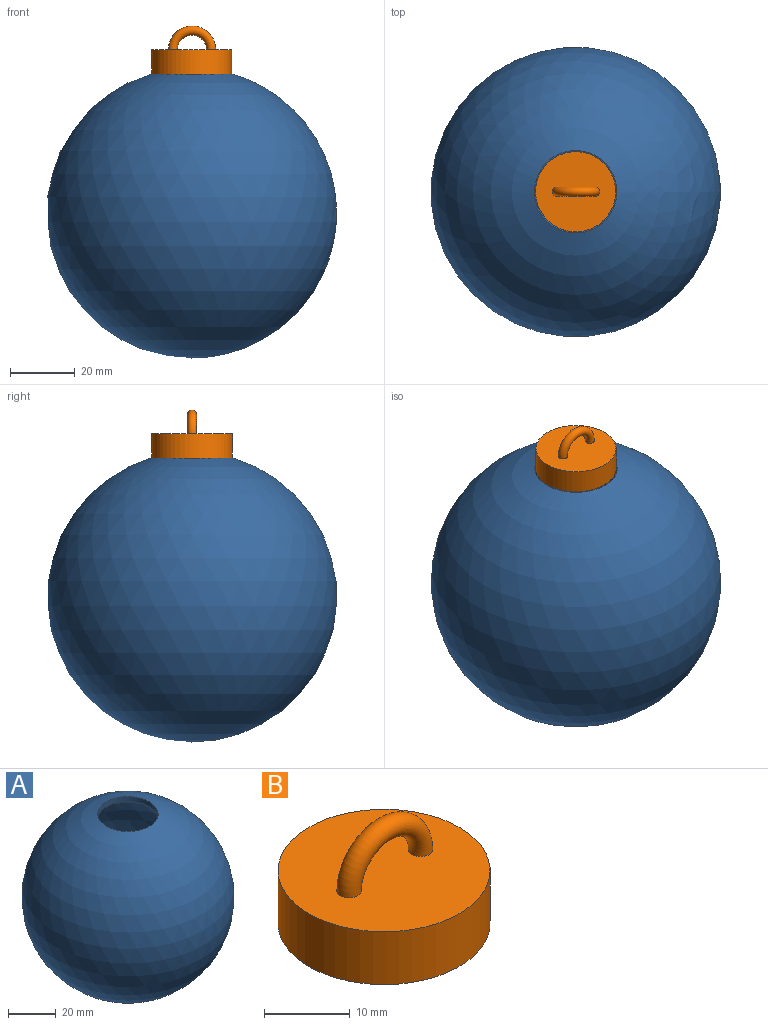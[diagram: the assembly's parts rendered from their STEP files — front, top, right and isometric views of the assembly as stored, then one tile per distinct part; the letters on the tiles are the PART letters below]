
ASSEMBLY  parts=2 mates=1
PART A: 3 faces, bbox 89.3x89.3x87.5 mm
  f0: sphere r=42.25mm, area 21911.1mm2, adj f2
  f1: sphere r=44.66mm, area 24548.8mm2, adj f2
  f2: cylinder r=12.7mm len=25.4mm, axis (0,0,1), area 201.4mm2, adj f0,f1
PART B: 4 faces, bbox 24.7x24.7x15.4 mm
  f0: plane 24.68x24.68mm, normal (0,0,1), area 465.8mm2, adj f1,f3
  f1: cylinder r=12.34mm len=24.68mm, axis (0,0,1), area 583.8mm2, adj f0,f2
  f2: plane 24.68x24.68mm, normal (0,0,-1), area 478.4mm2, adj f1
  f3: torus R=5.88mm, axis (0,-1,0), area 164.2mm2, adj f0
PLACE A t=(-2.1,0,3.79)mm
PLACE B at identity
MATE fastened A.f2 <-> B.f1  axis (0,0,1) through (-30.07,0,31.16)mm
